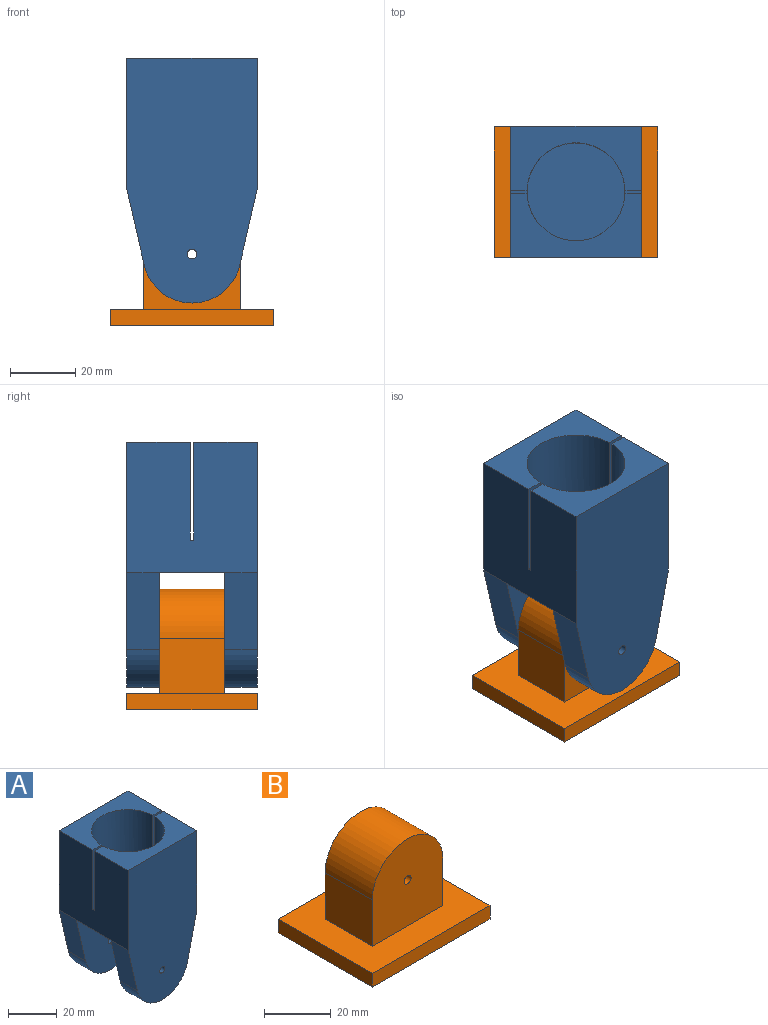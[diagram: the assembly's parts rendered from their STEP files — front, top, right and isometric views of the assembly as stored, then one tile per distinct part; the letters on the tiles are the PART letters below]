
ASSEMBLY  parts=2 mates=1
PART A: 25 faces, bbox 40x40x75 mm
  f0: plane 40x40mm, normal (-1,0,0), area 1570mm2, adj f1,f2,f3,f6,f8,f11,f13,f20
  f1: plane 40x19.5mm, normal (0,0,1), area 441.6mm2, adj f0,f6,f14,f15,f17,f20
  f2: plane 40x19.5mm, normal (0,0,1), area 441.6mm2, adj f0,f11,f14,f15,f18,f21
  f3: plane 23.37x10mm, normal (-0.97,0,-0.22), area 239.8mm2, adj f0,f4,f6,f7
  f4: cylinder r=15mm len=29.23mm, axis (0,-1,0), area 403.3mm2, adj f3,f5,f6,f7
  f5: plane 23.37x10mm, normal (0.97,0,-0.22), area 239.8mm2, adj f4,f6,f7,f14
  f6: plane 75x40mm, normal (0,1,0), area 2655.1mm2, adj f0,f1,f3,f4,f5,f14,f24
  f7: plane 40x35mm, normal (0,-1,0), area 1055.1mm2, adj f3,f4,f5,f13,f24
  f8: plane 23.37x10mm, normal (-0.97,0,-0.22), area 239.8mm2, adj f0,f9,f11,f12
  f9: cylinder r=15mm len=29.23mm, axis (0,1,0), area 403.3mm2, adj f8,f10,f11,f12
  f10: plane 23.37x10mm, normal (0.97,0,-0.22), area 239.8mm2, adj f9,f11,f12,f14
  f11: plane 75x40mm, normal (0,-1,0), area 2655.1mm2, adj f0,f2,f8,f9,f10,f14,f23
  f12: plane 40x35mm, normal (0,1,0), area 1055.1mm2, adj f8,f9,f10,f13,f23
  f13: plane 40x20mm, normal (0,0,-1), area 800mm2, adj f0,f7,f12,f14
  f14: plane 40x40mm, normal (1,0,0), area 1570mm2, adj f1,f2,f5,f6,f10,f11,f13,f17
  f15: cylinder r=15mm len=32mm, axis (0,0,1), area 2955.9mm2, adj f1,f2,f16,f17,f18,f19,f20,f21
  f16: plane 30x30mm, normal (0,0,1), area 706.9mm2, adj f15
  f17: plane 30x5.01mm, normal (0,-1,0), area 150.3mm2, adj f1,f14,f15,f19
  f18: plane 30x5.01mm, normal (0,1,0), area 150.3mm2, adj f2,f14,f15,f19
  f19: plane 5.01x1mm, normal (0,0,1), area 5mm2, adj f14,f15,f17,f18
  f20: plane 30x5.01mm, normal (0,-1,0), area 150.3mm2, adj f0,f1,f15,f22
  f21: plane 30x5.01mm, normal (0,1,0), area 150.3mm2, adj f0,f2,f15,f22
  f22: plane 5.01x1mm, normal (0,0,1), area 5mm2, adj f0,f15,f20,f21
  f23: cylinder r=1.5mm len=10mm, axis (0,-1,0), area 94.2mm2, adj f11,f12
  f24: cylinder r=1.5mm len=10mm, axis (0,-1,0), area 94.2mm2, adj f6,f7
PART B: 12 faces, bbox 50x40x37 mm
  f0: plane 40x5mm, normal (1,0,0), area 200mm2, adj f1,f3,f4,f5
  f1: plane 50x5mm, normal (0,1,0), area 250mm2, adj f0,f2,f4,f5
  f2: plane 40x5mm, normal (-1,0,0), area 200mm2, adj f1,f3,f4,f5
  f3: plane 50x5mm, normal (0,-1,0), area 250mm2, adj f0,f2,f4,f5
  f4: plane 50x40mm, normal (0,0,1), area 1400mm2, adj f0,f1,f2,f3,f6,f8,f9,f10
  f5: plane 50x40mm, normal (0,0,-1), area 2000mm2, adj f0,f1,f2,f3
  f6: plane 20x17mm, normal (1,0,0), area 340mm2, adj f4,f7,f9,f10
  f7: cylinder r=15mm len=30mm, axis (0,-1,0), area 942.5mm2, adj f6,f8,f9,f10
  f8: plane 20x17mm, normal (-1,0,0), area 340mm2, adj f4,f7,f9,f10
  f9: plane 32x30mm, normal (0,1,0), area 856.4mm2, adj f4,f6,f7,f8,f11
  f10: plane 32x30mm, normal (0,-1,0), area 856.4mm2, adj f4,f6,f7,f8,f11
  f11: cylinder r=1.5mm len=20mm, axis (0,-1,0), area 188.5mm2, adj f9,f10
PLACE A t=(-43.62,1.89,-0.38)mm
PLACE B t=(-43.62,1.89,-0.38)mm
MATE revolute B.f11 <-> A.f4  axis (0,-1,0) through (-43.62,-8.11,21.62)mm
